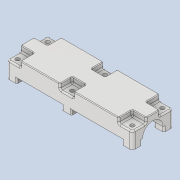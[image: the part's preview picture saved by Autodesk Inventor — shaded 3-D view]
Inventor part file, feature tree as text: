
AUTODESK INVENTOR PART (.ipt)
format: ipt  version: 2020.4 (Build 244396000, 396)  size: 779,264 bytes
history: native  units: mm
features: sketch x14, extrude x13, projected_geometry x9, fillet x3, other x1, mirror x1, boolean_combine x1
ambient origin geometry x8: Origin, YZ Plane, XZ Plane, XY Plane, X Axis, Y Axis, Z Axis, Center Point
bodies: Volumenkörper1 (feature_tree), Solid2 (feature_tree), Solid3 (feature_tree)
feature tree (42):
  extrude  "Extrusion1"  Depth=6.0mm
  other  "Spirale1"
  mirror  "Spiegeln1"
  extrude  "Extrusion5"  Depth=10.0mm
  extrude  "Extrusion6"  Depth=1.0mm
  boolean_combine  "Combine1"
  extrude  "Extrusion7"  Depth=10.0mm TaperAngle=0.0deg
  extrude  "Extrusion8"  Depth=100.0mm TaperAngle=0.0deg
  extrude  "Extrusion9"  Depth=24.0mm
  extrude  "Extrusion10"  Depth=12.0mm TaperAngle=0.0deg
  extrude  "Extrusion11"  Depth=4.0mm
  extrude  "Extrusion13"  Depth=10.0mm
  fillet  "Fillet2"  Radius=10.0mm
  fillet  "Fillet3"  Radius=77.15mm
  fillet  "Fillet4"  Radius=30.0mm
  extrude  "Extrusion14"  Depth=6.0mm
  extrude  "Extrusion15"  Depth=10.0mm TaperAngle=0.0deg
  extrude  "Extrusion16"  Depth=3.0mm
  extrude  "Extrusion17"  Depth=1.0mm
  sketch  "Skizze1"  dims[d0=6.0mm d1=11.0mm]
  sketch  "Skizze3"  dims[d2=36.0mm d3=0.0mm]
  projected_geometry  "Projizierte Kontur2"
  sketch  "Sketch7"  dims[d8=7.0mm d9=24.5mm d10=10.0mm d11=0.0mm d12=90.0deg d13=90.0deg d14=0.0mm d15=0.0mm d16=4.0mm]
  sketch  "Sketch8"  dims[d17=13.962634mm d18=1.0mm]
  sketch  "Sketch9"  dims[d19=0.1mm d32=10.0mm d33=0.0mm]
  projected_geometry  "Projected Loop4"
  sketch  "Sketch10"  dims[d34=7.0mm d35=100.0mm d36=0.0mm]
  sketch  "Sketch11"  dims[d37=82.0mm d38=0.0mm d39=24.0mm]
  projected_geometry  "Projected Loop5"
  projected_geometry  "Projected Loop6"
  sketch  "Sketch12"  dims[d40=30.0mm d41=12.0mm d42=0.0mm]
  sketch  "Sketch13"  dims[d43=3.0mm d44=4.0mm]
  projected_geometry  "Projected Loop7"
  projected_geometry  "Projected Loop8"
  sketch  "Sketch15"  dims[d45=4.0mm d46=20.0mm d48=22.0mm d49=20.0mm d51=84.0mm d54=10.0mm d55=0.0mm d56=77.15mm d57=30.0mm]
  sketch  "Sketch16"  dims[d62=4.0mm d63=0.0mm d64=6.0mm]
  projected_geometry  "Projected Loop10"
  sketch  "Sketch17"  dims[d65=10.0mm d66=0.0mm d67=10.0mm d68=0.0mm]
  projected_geometry  "Projected Loop11"
  projected_geometry  "Projected Loop12"
  sketch  "Sketch18"  dims[d76=3.0mm d77=3.0mm]
  sketch  "Sketch19"  dims[d78=4.0mm d79=48.0mm d80=46.0mm d81=4.0mm d85=7.0mm d86=6.9mm d87=3.5mm d88=7.0mm d89=6.9mm d90=3.5mm d91=10.0mm d92=10.0mm d93=10.0mm d94=10.0mm d95=10.0mm d96=10.0mm d97=10.0mm d98=10.0mm d99=10.0mm d100=10.0mm d101=10.0mm d102=10.0mm d103=4.0mm d104=0.0mm d105=1.0mm d106=1.0mm d107=2.0mm d108=0.5mm d109=6.5mm d110=2.1mm d111=0.0mm d112=6.5mm d113=2.1mm d114=0.0mm d115=180.0deg d116=6.9mm d117=6.9mm d118=6.9mm d119=6.9mm d120=12.0mm d121=0.2mm d122=0.0mm d123=15.0mm d124=0.2mm d125=0.0mm d126=7.9mm d127=0.0mm d128=7.9mm d129=0.0mm]
